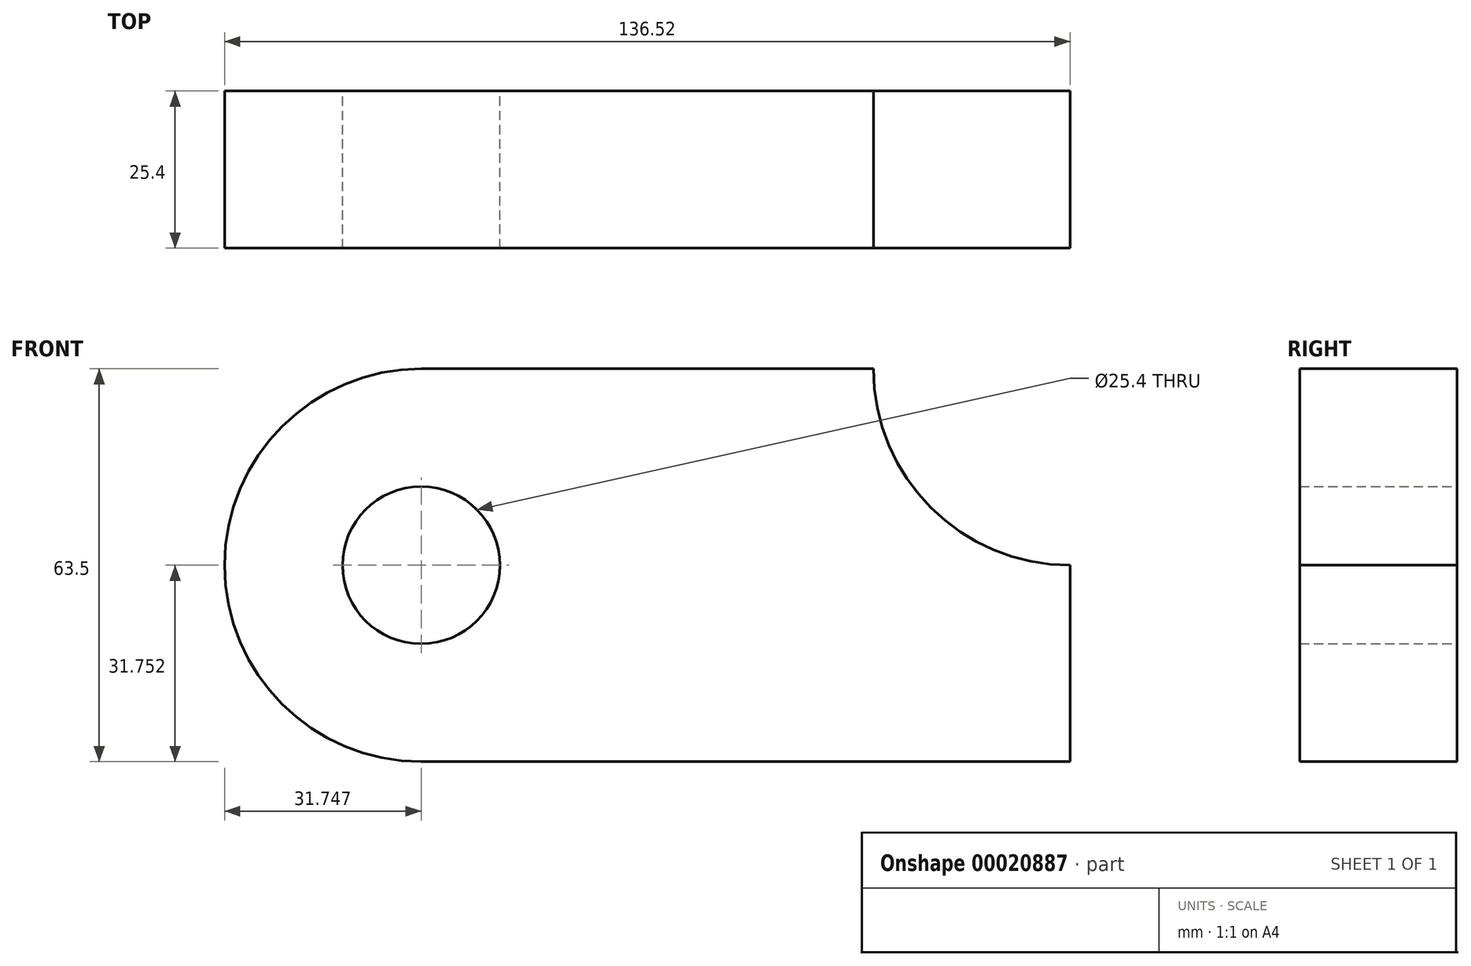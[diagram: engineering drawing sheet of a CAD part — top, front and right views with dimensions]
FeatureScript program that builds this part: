
annotation { "Feature Type Name" : "Feature", "Feature Type Description" : "" }
export const myFeature = defineFeature(function(context is Context, id is Id, definition is map)
    precondition{}
    {
        {
            var Q0;
            Q0=qCreatedBy(makeId("Front.planeOp"),FACE);
            var sketch = newSketch(context, id + "F0", { "sketchPlane" : qUnion([Q0])});
            skLineSegment(sketch, "E0.bottom", {"start": v(-54.5, 37.5) * mm, "end": v(50.28, 37.5) * mm});
            skLineSegment(sketch, "E0.top", {"start": v(-54.5, -26) * mm, "end": v(50.28, -26) * mm});
            skLineSegment(sketch, "E0.left", {"start": v(-54.5, 37.5) * mm, "end": v(-54.5, -26) * mm});
            skLineSegment(sketch, "E0.right", {"start": v(50.28, 37.5) * mm, "end": v(50.28, -26) * mm});
            skCircle(sketch, "E1", {"center": v(-54.5, 5.74) * mm, "radius": 31.75 * mm});
            skCircle(sketch, "E2", {"center": v(-54.5, 5.74) * mm, "radius": 12.7 * mm});
            skCircle(sketch, "E3", {"center": v(50.28, 37.5) * mm, "radius": 31.75 * mm});
            skSolve(sketch);
        }
        {
            var Q0;
            {var subQ6=sQuery(id+"F0.wireOp",EDGE,"E0.top");Q0=makeQuery(id+"F0.imprint","IMPRINT",FACE,{"disambiguationData":[TD([[makeQuery(id+"F0.imprint","IMPRINT",EDGE,{"derivedFrom":subQ6}),1.0]])]});}
            var Q1;
            {var subQ0=sQuery(id+"F0.wireOp",EDGE,"E2");var subQ1=sQuery(id+"F0.wireOp",EDGE,"E0.left");var subQ3=makeQuery(id+"F0.imprint","INTERSECT",VERTEX,{"disambiguationData":[OD(0.0)],"derivedFrom":[subQ1,subQ0]});Q1=makeQuery(id+"F0.imprint","IMPRINT",FACE,{"disambiguationData":[TD([[makeQuery(id+"F0.imprint","IMPRINT",EDGE,{"disambiguationData":[TD([[subQ3,1.0]])],"derivedFrom":subQ0}),-1.0]])]});}
            var Q2;
            {var subQ0=sQuery(id+"F0.wireOp",EDGE,"E2");var subQ1=sQuery(id+"F0.wireOp",EDGE,"E0.left");var subQ3=makeQuery(id+"F0.imprint","INTERSECT",VERTEX,{"disambiguationData":[OD(0.0)],"derivedFrom":[subQ1,subQ0]});Q2=makeQuery(id+"F0.imprint","IMPRINT",FACE,{"disambiguationData":[TD([[makeQuery(id+"F0.imprint","IMPRINT",EDGE,{"disambiguationData":[TD([[subQ3,-1.0]])],"derivedFrom":subQ0}),-1.0]])]});}
            extrude(context, id + "F1", {"entities" : qUnion([Q0, Q1, Q2]), "depth" : 25.4 * mm});
        }
    });
